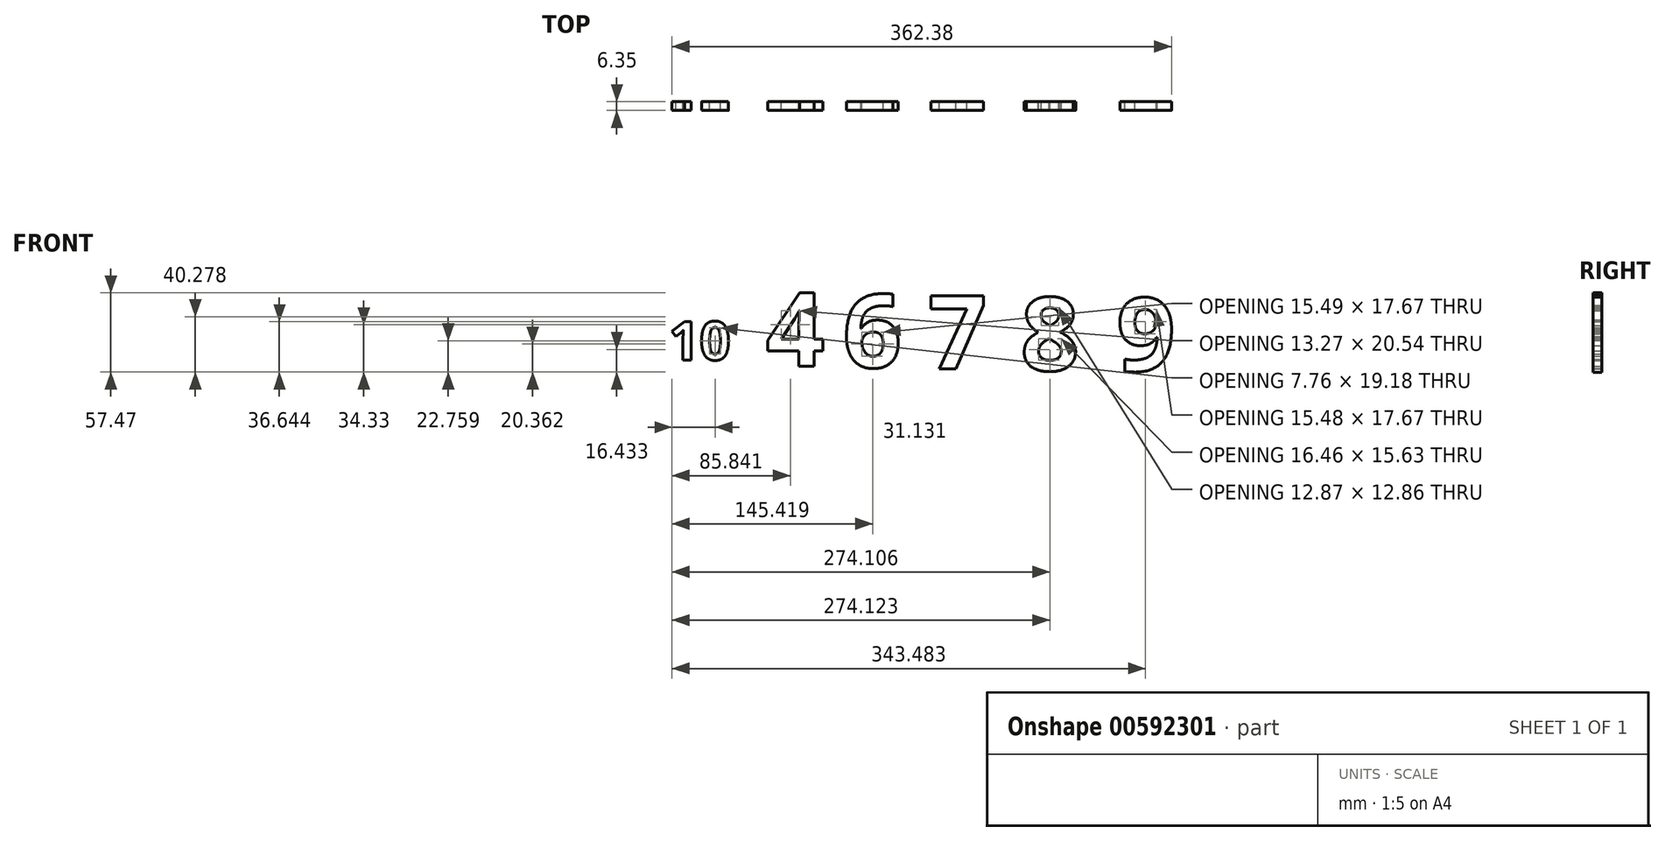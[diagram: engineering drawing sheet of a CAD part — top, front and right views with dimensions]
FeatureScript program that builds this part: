
annotation { "Feature Type Name" : "Feature", "Feature Type Description" : "" }
export const myFeature = defineFeature(function(context is Context, id is Id, definition is map)
    precondition{}
    {
        {
            var Q0;
            Q0=qCreatedBy(makeId("Front.planeOp"),FACE);
            var sketch = newSketch(context, id + "F0", { "sketchPlane" : qUnion([Q0])});
            skText(sketch, "E0", { "text": "4", "fontName": "OpenSans-Bold.ttf"});
            const initialGuessF0  = {"E0": [-0.11767, -0.0326, 1, 0, 0.0536]};
            skSetInitialGuess(sketch, initialGuessF0);
            skSolve(sketch);
        }
        {
            var Q0;
            Q0 = qSketchRegion(id + "F0", true);
            extrude(context, id + "F1", {"entities" : qUnion([Q0]), "depth" : 6.35 * mm, "offsetDistance" : 25.4 * mm});
        }
        {
            var Q0;
            Q0=qCreatedBy(makeId("Front.planeOp"),FACE);
            var sketch = newSketch(context, id + "F2", { "sketchPlane" : qUnion([Q0])});
            skText(sketch, "E1", { "text": "6", "fontName": "OpenSans-Bold.ttf"});
            const initialGuessF2  = {"E1": [-0.06182, -0.03364, 1, 0, 0.0536]};
            skSetInitialGuess(sketch, initialGuessF2);
            skSolve(sketch);
        }
        {
            var Q0;
            Q0 = qSketchRegion(id + "F2", true);
            extrude(context, id + "F3", {"entities" : qUnion([Q0]), "depth" : 6.35 * mm, "offsetDistance" : 25.4 * mm});
        }
        {
            var Q0;
            Q0=qCreatedBy(makeId("Front.planeOp"),FACE);
            var sketch = newSketch(context, id + "F4", { "sketchPlane" : qUnion([Q0])});
            skText(sketch, "E2", { "text": "7", "fontName": "OpenSans-Bold.ttf"});
            const initialGuessF4  = {"E2": [0, -0.03464, 1, 0, 0.0536]};
            skSetInitialGuess(sketch, initialGuessF4);
            skSolve(sketch);
        }
        {
            var Q0;
            Q0=makeQuery(id+"F4.imprint","IMPRINT",FACE,{"disambiguationData":[TD([[makeQuery(id+"F4.imprint","IMPRINT",EDGE,{"derivedFrom":sQuery(id+"F4.wireOp",EDGE,"E2.sketch_text.stroke-0")}),-1.0]])]});
            extrude(context, id + "F5", {"entities" : qUnion([Q0]), "depth" : 6.35 * mm, "offsetDistance" : 25.4 * mm});
        }
        {
            var Q0;
            Q0=qCreatedBy(makeId("Front.planeOp"),FACE);
            var sketch = newSketch(context, id + "F6", { "sketchPlane" : qUnion([Q0])});
            skText(sketch, "E3", { "text": "8", "fontName": "OpenSans-Bold.ttf"});
            const initialGuessF6  = {"E3": [0.06714, -0.03583, 1, 0, 0.0536]};
            skSetInitialGuess(sketch, initialGuessF6);
            skSolve(sketch);
        }
        {
            var Q0;
            Q0 = qSketchRegion(id + "F6", true);
            extrude(context, id + "F7", {"entities" : qUnion([Q0]), "depth" : 6.35 * mm, "offsetDistance" : 25.4 * mm});
        }
        {
            var Q0;
            Q0=qCreatedBy(makeId("Front.planeOp"),FACE);
            var sketch = newSketch(context, id + "F8", { "sketchPlane" : qUnion([Q0])});
            skText(sketch, "E4", { "text": "9", "fontName": "OpenSans-Bold.ttf"});
            const initialGuessF8  = {"E4": [0.13675, -0.03619, 1, 0, 0.0536]};
            skSetInitialGuess(sketch, initialGuessF8);
            skSolve(sketch);
        }
        {
            var Q0;
            Q0 = qSketchRegion(id + "F8", true);
            extrude(context, id + "F9", {"entities" : qUnion([Q0]), "depth" : 6.35 * mm, "offsetDistance" : 25.4 * mm});
        }
        {
            var Q0;
            Q0=qCreatedBy(makeId("Front.planeOp"),FACE);
            var sketch = newSketch(context, id + "F10", { "sketchPlane" : qUnion([Q0])});
            skText(sketch, "E5", { "text": "10", "fontName": "OpenSans-Bold.ttf"});
            const initialGuessF10  = {"E5": [-0.18803, -0.02812, 1, 0, 0.02812]};
            skSetInitialGuess(sketch, initialGuessF10);
            skSolve(sketch);
        }
        {
            var Q0;
            Q0 = qSketchRegion(id + "F10", true);
            extrude(context, id + "F11", {"entities" : qUnion([Q0]), "depth" : 6.35 * mm, "offsetDistance" : 25.4 * mm});
        }
    });
